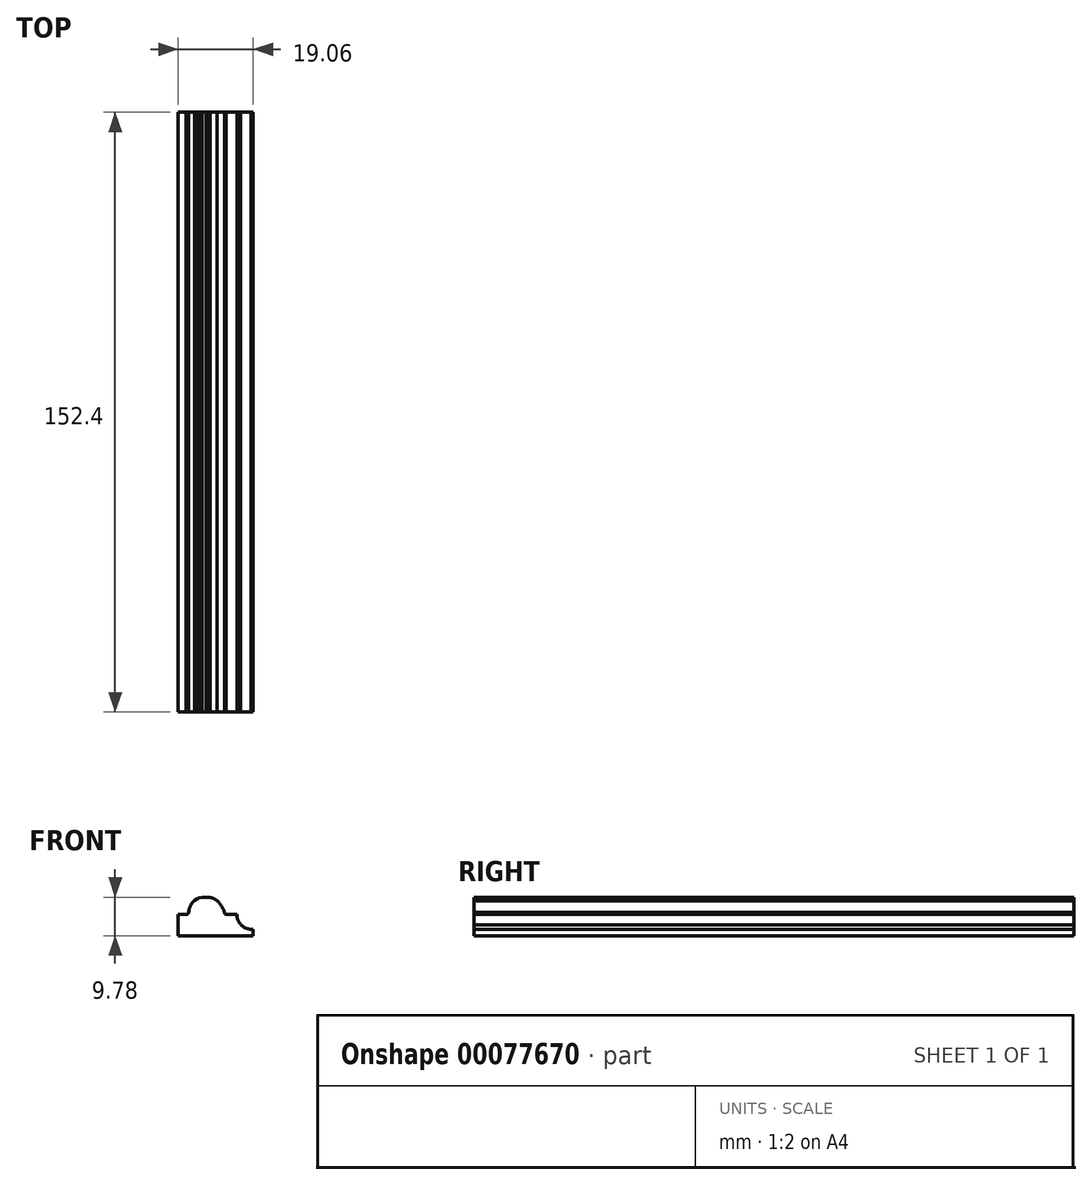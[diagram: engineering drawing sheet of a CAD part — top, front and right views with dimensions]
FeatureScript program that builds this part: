
annotation { "Feature Type Name" : "Feature", "Feature Type Description" : "" }
export const myFeature = defineFeature(function(context is Context, id is Id, definition is map)
    precondition{}
    {
        {
            var Q0;
            Q0=qCreatedBy(makeId("Front.planeOp"),FACE);
            var sketch = newSketch(context, id + "F0", { "sketchPlane" : qUnion([Q0])});
            skLineSegment(sketch, "E0", {"start": v(-9.53, -4.89) * mm, "end": v(-9.53, 0.5) * mm});
            skLineSegment(sketch, "E1", {"start": v(-1.7, 4.83) * mm, "end": v(-2.41, 4.89) * mm});
            skArc(sketch, "E2", {"start": v(6.38, -2.1) * mm, "mid": v(7.58, -2.95) * mm, "end": v(9, -3.31) * mm});
            skArc(sketch, "E3", {"start": v(5.4, 0.48) * mm, "mid": v(5.62, -0.91) * mm, "end": v(6.38, -2.1) * mm});
            skLineSegment(sketch, "E4", {"start": v(5.4, 0.48) * mm, "end": v(2.6, 0.48) * mm});
            skArc(sketch, "E5", {"start": v(0.4, 3.92) * mm, "mid": v(-0.45, 4.5) * mm, "end": v(-1.43, 4.8) * mm});
            skLineSegment(sketch, "E6", {"start": v(-1.43, 4.8) * mm, "end": v(-1.7, 4.84) * mm});
            skArc(sketch, "E7", {"start": v(2.2, 0.98) * mm, "mid": v(1.52, 2.6) * mm, "end": v(0.4, 3.92) * mm});
            skArc(sketch, "E8", {"start": v(2.2, 0.98) * mm, "mid": v(2.31, 0.66) * mm, "end": v(2.6, 0.48) * mm});
            skArc(sketch, "E9", {"start": v(-5.33, 4.1) * mm, "mid": v(-6.26, 3.02) * mm, "end": v(-6.75, 1.69) * mm});
            skLineSegment(sketch, "E10", {"start": v(-4.16, 4.71) * mm, "end": v(-4.8, 4.46) * mm});
            skLineSegment(sketch, "E11", {"start": v(-2.41, 4.89) * mm, "end": v(-3.43, 4.89) * mm});
            skLineSegment(sketch, "E12", {"start": v(-3.43, 4.89) * mm, "end": v(-4.16, 4.71) * mm});
            skLineSegment(sketch, "E13", {"start": v(-4.8, 4.46) * mm, "end": v(-5.33, 4.1) * mm});
            skLineSegment(sketch, "E14", {"start": v(-6.75, 1.69) * mm, "end": v(-6.88, 0.98) * mm});
            skArc(sketch, "E15", {"start": v(-7.47, 0.5) * mm, "mid": v(-7.07, 0.62) * mm, "end": v(-6.88, 0.98) * mm});
            skLineSegment(sketch, "E16", {"start": v(-9.53, 0.5) * mm, "end": v(-9.53, -4.89) * mm});
            skLineSegment(sketch, "E17", {"start": v(9.53, -4.89) * mm, "end": v(-9.53, -4.89) * mm});
            skLineSegment(sketch, "E18", {"start": v(-7.47, 0.5) * mm, "end": v(-9.53, 0.5) * mm});
            skLineSegment(sketch, "E19", {"start": v(9, -3.31) * mm, "end": v(9.53, -3.31) * mm});
            skLineSegment(sketch, "E20", {"start": v(9.53, -3.31) * mm, "end": v(9.53, -4.89) * mm});
            skSolve(sketch);
        }
        {
            var Q0;
            {var subQ0=sQuery(id+"F0.wireOp",EDGE,"E1");Q0=makeQuery(id+"F0.imprint","IMPRINT",FACE,{"disambiguationData":[TD([[makeQuery(id+"F0.imprint","IMPRINT",EDGE,{"derivedFrom":subQ0}),1.0]])]});}
            extrude(context, id + "F1", {"entities" : qUnion([Q0]), "depth" : 152.4 * mm});
        }
    });
